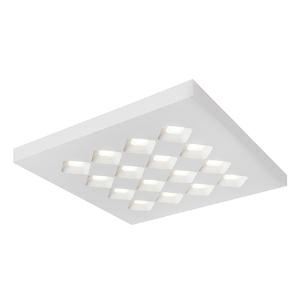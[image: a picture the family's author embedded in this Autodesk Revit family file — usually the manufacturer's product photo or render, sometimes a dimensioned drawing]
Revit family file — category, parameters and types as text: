
# Revit family: 3f_filippi_-_3f_diagon_p_soft_ugr_tunable_white_3f_filippi_-_12142_-_3f_diagon_p_25w_dt8_tw_soft_ugr_596_a8409424da2a3a25
name_source: partatom
category: Lighting Fixtures
units: mm (PartAtom-declared; Revit-internal decimal feet)

## family parameters
Cut with Voids When Loaded = No
Host = Face
Light Source = No
Part Type = Normal
Room Calculation Point = No
Round Connector Dimension = Use Diameter
Shared = No

## types (1)
- 3F Filippi - 3F Dìagon P Soft UGR Tunable White (1 x LED, 3567 lm, 30 W, 2700 K)
    Apparent Load = 30 VA
    Approval mark = ENEC
    CIE Flux Codes = 59 92 100 100 100
    Color Rendering = 80
    Color Temperature = 2700 K
    Control Gear = Electronic transformer
    Default Elevation = 1800 mm
    Description = ILLUMINOTECHNICAL
Luminous efficiency 100% (DLOR 100%, ULOR 0%).
Initial luminous flux of the luminaire 3567 lm.
Direct symmetric distribution.
Installation Interdistance Transv.D = 1.23 x hu - Long.D = 1.23 x hu.
Average luminance <3000 cd/m² for radial angles >65°.
Tabular UGR (CIE 117 - 4H-8H; S=0.25H; 70/50/20): RUG 18.6 - 18.6.
Beam angle: 102° - 101°.
Luminous efficacy 119 lm/W.
Lifetime (L95/B10): 30000 h. (tq+25°C)
Lifetime (L90/B10): 50000 h. (tq+25°C)
Lifetime (L80/B10): 80000 h. (tq+25°C)
Lifetime (L75/B10): 100000 h. (tq+25°C)
Sudden decreased luminous flux after 50000 hours: 0% (C0).
Photobiological safety in compliance with IEC/TR 62778: RG0 risk exempt, (IEC 62471).
In compliance with IEC/EN 62722-2-1 - IEC/EN 62717 standards.

SOURCE
Squared LED module 25W/TW.
Energy efficiency class (UE 2019/2020 - UE 2019/2015): D.
CIE 13.3 Colour rendering index: CRI >80 (R9 <50%).
IES TM-30 Fidelity Index: Rf = 84 Rg = 95.
The colour temperature can be adjusted between 2700 K and 6500 K.
Colour initial tolerance (MacAdam): SDCM 3.

MECHANICAL
White painted frame.
Height only 40 mm.
Housing in hot-galvanised steel, painted in white polyester.
Honeycombed diagonal screen in white anti-glare polycarbonate.
Opal methacrylate (PMMA) rhomboid lenses with differentiated, engraved and prismatic surfaces for diffused, soft lighting and excellent visual comfort.
Luminaire with limited surface temperature. - D - (EN 60598-2-24)
Dimensions: 596x596 mm, height 40 mm. Weight 6.825 kg.
IP40 protection degree.
Mechanical strength to impacts IK06 (1 joule).
Glow-wire test resistance 650°C.

ELECTRICAL
Halogen Free DALI DT8, PUSH-DIM, electronic wiring 230V-50/60Hz, power factor 0.90 at full load, THD <25%, constant output current, class I, 1 driver, 1 DALI addresse.
Power of the luminaire 30 W.
CE - IEC 60598-1 - EN 60598-1.
SAFE FLICKER: PstLM=<1 and SVM=<0.4 (IEC TR 61547-1 and IEC TR 63158), to ensure a more comfortable and safe light.
Luminaire compliant with EN 60598-2-22 for power supply from a centralised emergency system CPSS (Central Power Supply System), not incorporated in the luminaire - high risk areas excluded. The default power and flux are 100% in AC and 15% in DC.
Ambient temperature from 0°C to +25°C.
Temperature class T6 max 85°C.
5-pole terminal block (L-N-PE-DA/DA) quick connection for line connection with connection capacity 2x2.5 mm² per poles.
Relative humidity UR: <85%.

INSTALLATION
Ceiling.

APPLICATIONS
Any environments requiring light which aims for the wellness of people.
Environments: staterooms, with VDTs, offices.
Environments with exacting visual tasks, where diffused soft light for optimum visual comfort is required.

LIGHT MANAGEMENT
Recommended minimum setting: 10%.
The luminaire, equipped with DALI DT8 driver, is designed for adjusting the luminous flux and colour temperature; can be controlled manually or automatically/manually with 3F HCL technology or 3F Bluetooth.

WARNING
Luminaire designed for disposal/recycling at end-of-life.
Replaceable (LED only) light source by a professional. Replaceable control gear by a professional.
    Height = 40 mm  [stored 0.131234 ft]
    Lamp = 1 x LED
    Lamp Light Flux = 3567 lm
    Lamp Power = 30 W
    Lamp count = 1
    Length = 596 mm
    Lifetime = 50000 h
    Luminous efficacy = 119 lm/W
    Manufacturer = 3F Filippi
    ModVariant = No
    Model = 3F Filippi - 12142 - 3F Diagon P 25W DT8 TW SOFT UGR 596x596 (CCT 2700)
    Mounting Place = Ceiling
    Mounting Type = Surface mounted
    Number of Poles = 1
    OnlyDefault = Yes
    Power Factor = 1
    Product Name = 3F Filippi - 3F Dìagon P Soft UGR Tunable White
    Product group = ceiling mounted luminaire
    ProductGroupID = 3
    Protection Class = Protection class I
    Protection Degree = IP 40
    RLX_Detail_Level = 1
    RLX_Emergency_Light_Flux = 0 lm
    RLX_Emergency_Type = 0
    RLX_Emergency_Type_DB = No
    RlxData = <blob elided: 96661 chars, md5=5a70699d>
    Socket = socket
    Standby Power = 0 W
    System Light Flux = 3567 lm
    System Power = 30 W
    Type Comments = Product without accessories
    Type Image = 3ffilippi_3f_diagon_p_soft_ugr_tunable_white.jpg
    URL = http://relux.com
    VarID = ---
    Voltage = 0 V
    Weight = 0.00 kg
    Width = 596 mm

note: [stored X ft] marks values corroborated as IEEE doubles in the binary element streams (Revit-internal decimal feet)

## geometry (parser evidence)
native form markers: Blend x4, Sweep x12
no freeform markers — native parametric forms only
